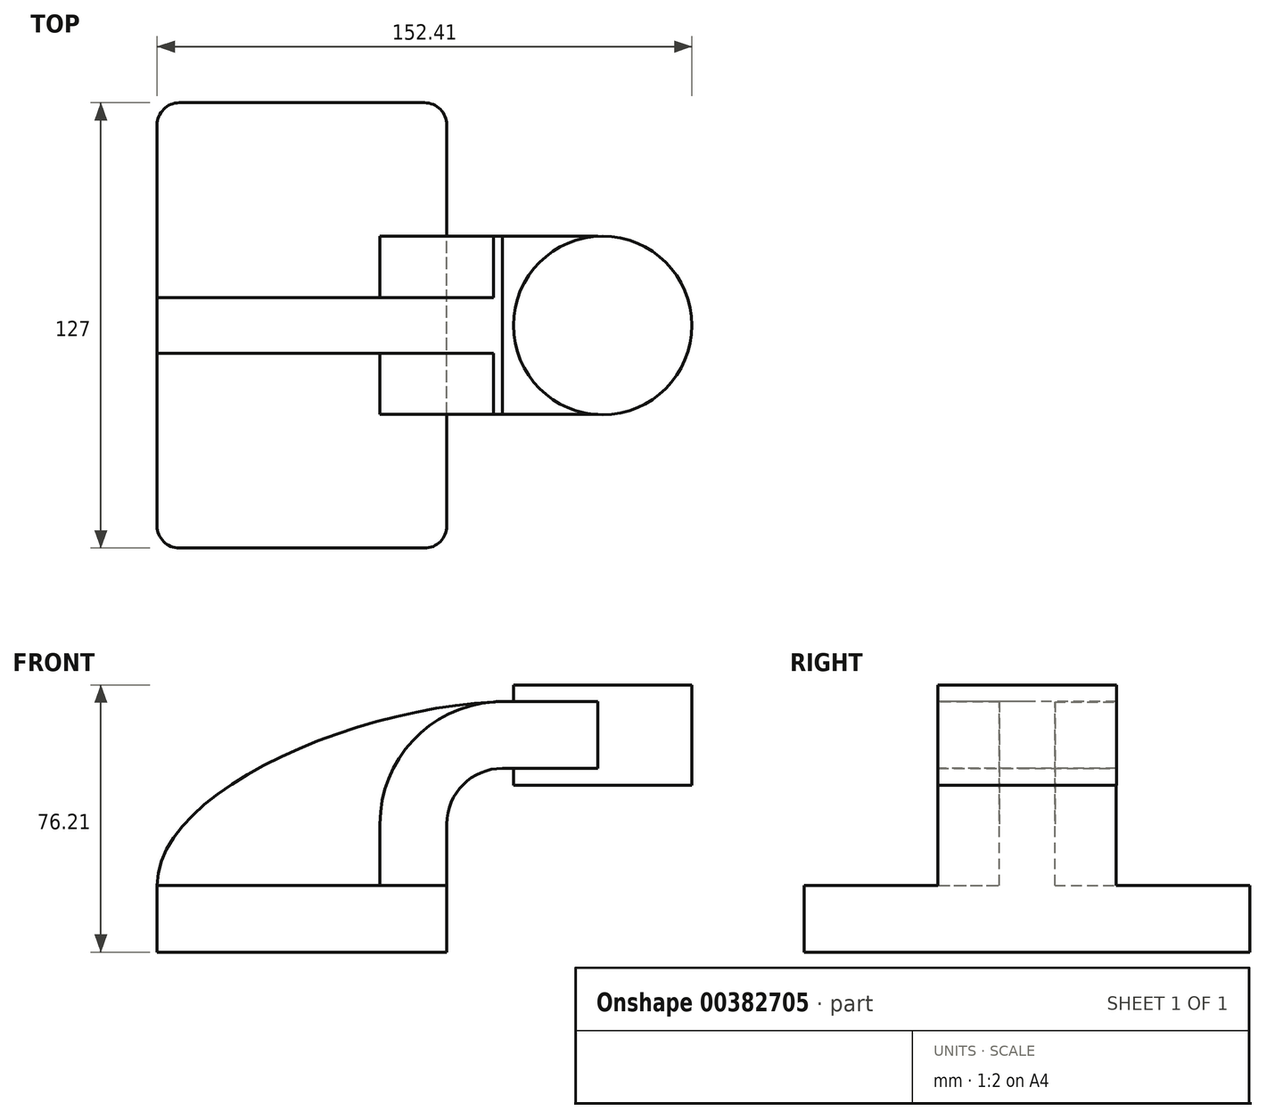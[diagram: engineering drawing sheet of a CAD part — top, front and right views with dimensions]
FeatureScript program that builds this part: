
annotation { "Feature Type Name" : "Feature", "Feature Type Description" : "" }
export const myFeature = defineFeature(function(context is Context, id is Id, definition is map)
    precondition{}
    {
        {
            var Q0;
            Q0=qCreatedBy(makeId("Front.planeOp"),FACE);
            var sketch = newSketch(context, id + "F0", { "sketchPlane" : qUnion([Q0])});
            skLineSegment(sketch, "E0.bottom", {"start": v(-41.28, 9.52) * mm, "end": v(41.27, 9.53) * mm});
            skLineSegment(sketch, "E0.top", {"start": v(-41.28, -9.53) * mm, "end": v(41.28, -9.53) * mm});
            skLineSegment(sketch, "E0.left", {"start": v(-41.28, 9.52) * mm, "end": v(-41.28, -9.53) * mm});
            skLineSegment(sketch, "E0.right", {"start": v(41.28, 9.53) * mm, "end": v(41.28, -9.52) * mm});
            skPoint(sketch, "E0.middle", {"position": v(0, 0) * mm});
            skLineSegment(sketch, "E1.bottom", {"start": v(60.32, 38.1) * mm, "end": v(111.12, 38.1) * mm});
            skLineSegment(sketch, "E1.top", {"start": v(60.32, 66.68) * mm, "end": v(111.12, 66.68) * mm});
            skLineSegment(sketch, "E1.left", {"start": v(60.32, 38.1) * mm, "end": v(60.32, 66.67) * mm});
            skLineSegment(sketch, "E1.right", {"start": v(111.12, 38.1) * mm, "end": v(111.12, 66.68) * mm});
            skPoint(sketch, "E1.middle", {"position": v(85.72, 52.39) * mm});
            skLineSegment(sketch, "E2", {"start": v(41.27, 9.53) * mm, "end": v(41.27, 27) * mm});
            skArc(sketch, "E3", {"start": v(41.27, 27) * mm, "mid": v(45.92, 38.23) * mm, "end": v(57.15, 42.88) * mm});
            skLineSegment(sketch, "E4", {"start": v(57.15, 42.88) * mm, "end": v(85.68, 42.88) * mm});
            skLineSegment(sketch, "E5.0", {"start": v(57.15, 61.93) * mm, "end": v(85.68, 61.93) * mm});
            skArc(sketch, "E5.1", {"start": v(22.22, 27) * mm, "mid": v(32.45, 51.7) * mm, "end": v(57.15, 61.93) * mm});
            skLineSegment(sketch, "E5.2", {"start": v(22.22, 9.53) * mm, "end": v(22.22, 27) * mm});
            skLineSegment(sketch, "E6", {"start": v(85.68, 42.88) * mm, "end": v(85.68, 66.68) * mm});
            skFitSpline(sketch, "E7", {"points": [v(-41.28, 9.52) * mm, v(57.15, 61.93) * mm], "startDerivative": vector(0.02, 81.9) * mm, "endDerivative": vector(120.73, 3.1) * mm});
            skLineSegment(sketch, "E8", {"start": v(85.68, 42.88) * mm, "end": v(85.68, 38.1) * mm});
            skSolve(sketch);
        }
        {
            var Q0;
            Q0=makeQuery(id+"F0.imprint","IMPRINT",FACE,{"disambiguationData":[TD([[makeQuery(id+"F0.imprint","IMPRINT",EDGE,{"derivedFrom":sQuery(id+"F0.wireOp",EDGE,"E0.top")}),1.0]])]});
            extrude(context, id + "F1", {"entities" : qUnion([Q0]), "endBound" : BoundingType.SYMMETRIC, "depth" : 127 * mm});
        }
        {
            var Q0;
            {var subQ6=sQuery(id+"F0.wireOp",EDGE,"E2");Q0=makeQuery(id+"F0.imprint","IMPRINT",FACE,{"disambiguationData":[TD([[makeQuery(id+"F0.imprint","IMPRINT",EDGE,{"derivedFrom":subQ6}),1.0]])]});}
            var Q1;
            {var subQ0=sQuery(id+"F0.wireOp",EDGE,"E4");var subQ1=sQuery(id+"F0.wireOp",EDGE,"E1.left");var subQ2=makeQuery(id+"F0.imprint","INTERSECT",VERTEX,{"derivedFrom":[subQ1,subQ0]});Q1=makeQuery(id+"F0.imprint","IMPRINT",FACE,{"disambiguationData":[TD([[makeQuery(id+"F0.imprint","IMPRINT",EDGE,{"disambiguationData":[TD([[subQ2,-1.0]])],"derivedFrom":subQ1}),-1.0]])]});}
            extrude(context, id + "F2", {"entities" : qUnion([Q0, Q1]), "operationType" : NewBodyOperationType.ADD, "endBound" : BoundingType.SYMMETRIC, "depth" : 50.8 * mm});
        }
        {
            var Q0;
            {var subQ3=sQuery(id+"F0.wireOp",EDGE,"E5.2");Q0=makeQuery(id+"F0.imprint","IMPRINT",FACE,{"disambiguationData":[TD([[makeQuery(id+"F0.imprint","IMPRINT",EDGE,{"derivedFrom":subQ3}),1.0]])]});}
            extrude(context, id + "F3", {"entities" : qUnion([Q0]), "operationType" : NewBodyOperationType.ADD, "endBound" : BoundingType.SYMMETRIC, "depth" : 15.88 * mm});
        }
        {
            var Q0;
            {var subQ3=sQuery(id+"F0.wireOp",EDGE,"E1.right");Q0=makeQuery(id+"F0.imprint","IMPRINT",FACE,{"disambiguationData":[TD([[makeQuery(id+"F0.imprint","IMPRINT",EDGE,{"derivedFrom":subQ3}),1.0]])]});}
            var Q1;
            Q1=sQuery(id+"F0.wireOp",EDGE,"E6");
            revolve(context, id + "F4", {"operationType" : NewBodyOperationType.ADD, "entities" : qUnion([Q0]), "axis" : qUnion([Q1]), "revolveType" : RevolveType.FULL});
        }
        {
            var Q0;
            Q0=makeQuery(id+"F1.opExtrude","CAP_EDGE",EDGE,{"disambiguationData":[OSD([sQuery(id+"F0.wireOp",EDGE,"E0.right")])],"isStart":false});
            var Q1;
            Q1=makeQuery(id+"F1.opExtrude","CAP_EDGE",EDGE,{"disambiguationData":[OSD([sQuery(id+"F0.wireOp",EDGE,"E0.left")])],"isStart":false});
            var Q2;
            Q2=makeQuery(id+"F1.opExtrude","CAP_EDGE",EDGE,{"disambiguationData":[OSD([sQuery(id+"F0.wireOp",EDGE,"E0.right")])],"isStart":true});
            var Q3;
            Q3=makeQuery(id+"F1.opExtrude","CAP_EDGE",EDGE,{"disambiguationData":[OSD([sQuery(id+"F0.wireOp",EDGE,"E0.left")])],"isStart":true});
            fillet(context, id + "F5", {"entities" : qUnion([Q0, Q1, Q2, Q3]), "radius" : 6.35 * mm, "tangentPropagation" : true, "allowEdgeOverflow" : false});
        }
    });
